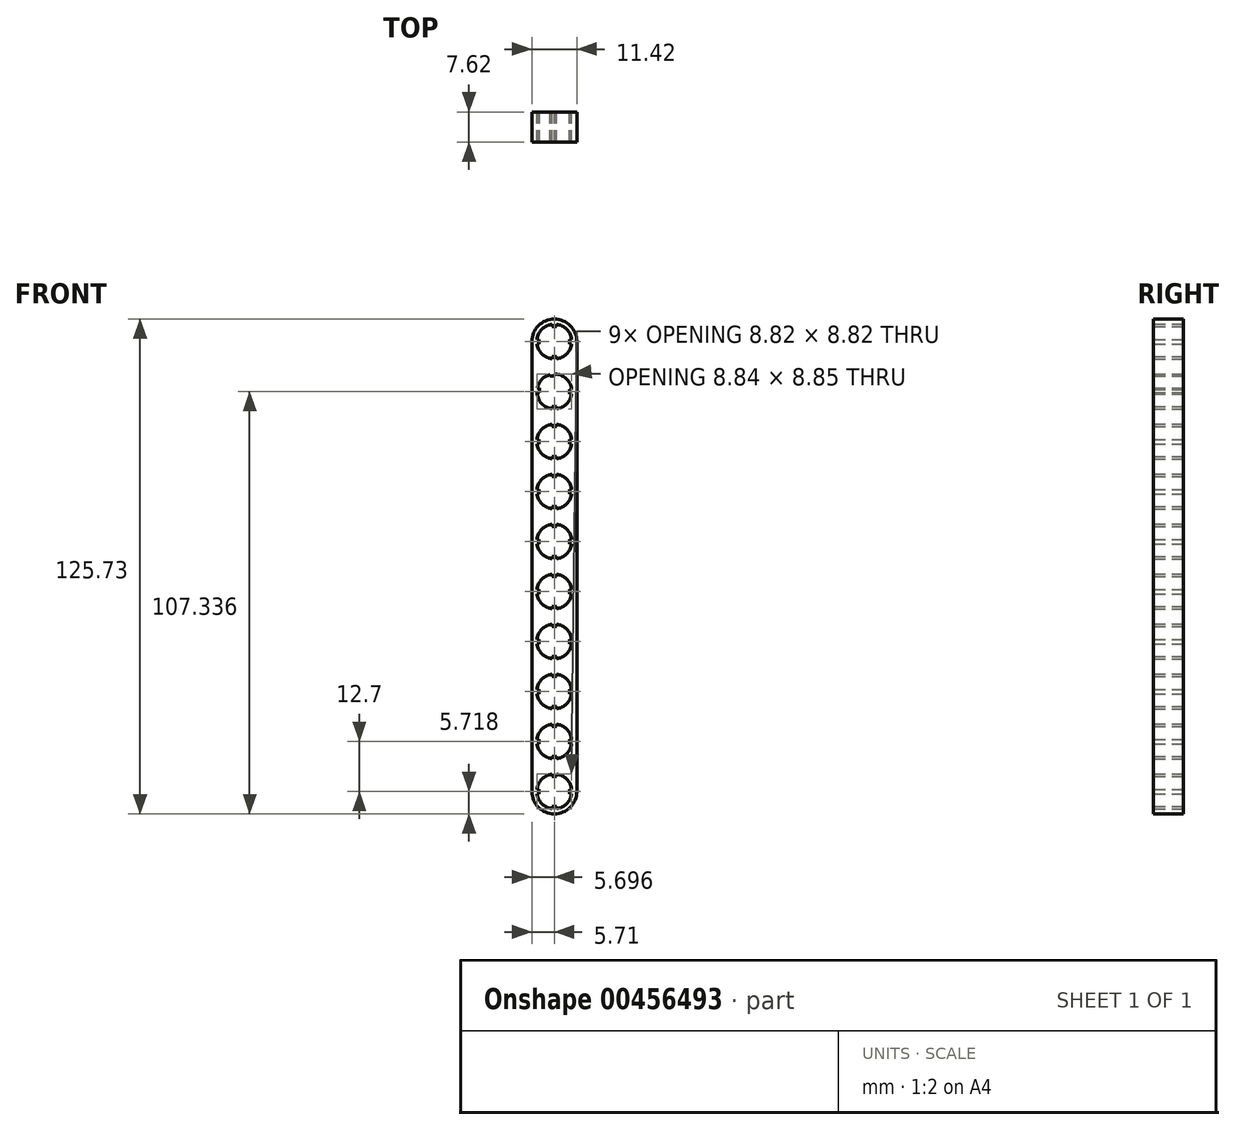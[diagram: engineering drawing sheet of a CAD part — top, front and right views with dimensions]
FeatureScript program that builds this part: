
annotation { "Feature Type Name" : "Feature", "Feature Type Description" : "" }
export const myFeature = defineFeature(function(context is Context, id is Id, definition is map)
    precondition{}
    {
        {
            var Q0;
            Q0=qCreatedBy(makeId("Front.planeOp"),FACE);
            var sketch = newSketch(context, id + "F0", { "sketchPlane" : qUnion([Q0])});
            skCircle(sketch, "E0", {"center": v(0, 47.45) * mm, "radius": 4.45 * mm});
            skCircle(sketch, "E1", {"center": v(0, 34.75) * mm, "radius": 4.45 * mm});
            skCircle(sketch, "E2", {"center": v(0, 22.05) * mm, "radius": 4.45 * mm});
            skCircle(sketch, "E3", {"center": v(0, 9.35) * mm, "radius": 4.45 * mm});
            skCircle(sketch, "E4", {"center": v(0, -3.35) * mm, "radius": 4.45 * mm});
            skCircle(sketch, "E5", {"center": v(0, -16.05) * mm, "radius": 4.45 * mm});
            skCircle(sketch, "E6", {"center": v(0, -28.75) * mm, "radius": 4.45 * mm});
            skCircle(sketch, "E7", {"center": v(0, -41.45) * mm, "radius": 4.45 * mm});
            skCircle(sketch, "E8", {"center": v(0, -54.15) * mm, "radius": 4.45 * mm});
            skCircle(sketch, "E9", {"center": v(0, -66.85) * mm, "radius": 4.45 * mm});
            skCircle(sketch, "E10", {"center": v(0, 47.45) * mm, "radius": 5.72 * mm});
            skCircle(sketch, "E11", {"center": v(0, 34.75) * mm, "radius": 5.72 * mm});
            skCircle(sketch, "E12", {"center": v(0, 22.05) * mm, "radius": 5.72 * mm});
            skCircle(sketch, "E13", {"center": v(0, 9.35) * mm, "radius": 5.72 * mm});
            skCircle(sketch, "E14", {"center": v(0, -3.35) * mm, "radius": 5.72 * mm});
            skCircle(sketch, "E15", {"center": v(0, -16.05) * mm, "radius": 5.72 * mm});
            skCircle(sketch, "E16", {"center": v(0, -28.75) * mm, "radius": 5.72 * mm});
            skCircle(sketch, "E17", {"center": v(0, -41.45) * mm, "radius": 5.72 * mm});
            skCircle(sketch, "E18", {"center": v(0, -54.15) * mm, "radius": 5.72 * mm});
            skCircle(sketch, "E19", {"center": v(0, -66.85) * mm, "radius": 5.72 * mm});
            skLineSegment(sketch, "E20", {"start": v(-5.72, 47.45) * mm, "end": v(-5.71, -66.85) * mm});
            skLineSegment(sketch, "E21", {"start": v(5.72, 47.45) * mm, "end": v(5.72, -66.85) * mm});
            skLineSegment(sketch, "E22", {"start": v(-0.57, 51.86) * mm, "end": v(-0.57, 51.3) * mm});
            skLineSegment(sketch, "E23", {"start": v(-0.57, 51.3) * mm, "end": v(0.57, 51.3) * mm});
            skLineSegment(sketch, "E24", {"start": v(0.57, 51.3) * mm, "end": v(0.57, 51.86) * mm});
            skLineSegment(sketch, "E25", {"start": v(4.4, 48.02) * mm, "end": v(3.85, 48.02) * mm});
            skLineSegment(sketch, "E26", {"start": v(3.85, 48.02) * mm, "end": v(3.85, 46.88) * mm});
            skLineSegment(sketch, "E27", {"start": v(3.85, 46.88) * mm, "end": v(4.4, 46.88) * mm});
            skLineSegment(sketch, "E28", {"start": v(-0.57, 43.04) * mm, "end": v(-0.57, 43.6) * mm});
            skLineSegment(sketch, "E29", {"start": v(-0.57, 43.6) * mm, "end": v(0.57, 43.6) * mm});
            skLineSegment(sketch, "E30", {"start": v(0.57, 43.6) * mm, "end": v(0.57, 43.04) * mm});
            skLineSegment(sketch, "E31", {"start": v(-4.4, 48.02) * mm, "end": v(-3.85, 48.02) * mm});
            skLineSegment(sketch, "E32", {"start": v(-3.85, 48.02) * mm, "end": v(-3.85, 46.88) * mm});
            skLineSegment(sketch, "E33", {"start": v(-3.85, 46.88) * mm, "end": v(-4.4, 46.88) * mm});
            skLineSegment(sketch, "E34", {"start": v(-4.5, -15.48) * mm, "end": v(-3.85, -15.48) * mm});
            skLineSegment(sketch, "E35", {"start": v(-3.85, -15.48) * mm, "end": v(-3.85, -16.62) * mm});
            skLineSegment(sketch, "E36", {"start": v(-3.85, -16.62) * mm, "end": v(-4.4, -16.62) * mm});
            skLineSegment(sketch, "E37", {"start": v(4.4, 9.92) * mm, "end": v(3.85, 9.92) * mm});
            skLineSegment(sketch, "E38", {"start": v(3.85, 9.92) * mm, "end": v(3.85, 8.78) * mm});
            skLineSegment(sketch, "E39", {"start": v(3.85, 8.78) * mm, "end": v(4.4, 8.78) * mm});
            skLineSegment(sketch, "E40", {"start": v(4.4, -66.28) * mm, "end": v(3.85, -66.28) * mm});
            skLineSegment(sketch, "E41", {"start": v(3.85, -66.28) * mm, "end": v(3.85, -67.42) * mm});
            skLineSegment(sketch, "E42", {"start": v(3.85, -67.42) * mm, "end": v(4.4, -67.42) * mm});
            skLineSegment(sketch, "E43", {"start": v(-1.06, 39.07) * mm, "end": v(-1.06, 38.63) * mm});
            skLineSegment(sketch, "E44", {"start": v(-1.06, 38.63) * mm, "end": v(0.09, 38.63) * mm});
            skLineSegment(sketch, "E45", {"start": v(0.09, 38.63) * mm, "end": v(0.09, 39.2) * mm});
            skLineSegment(sketch, "E46", {"start": v(-4.36, 35.61) * mm, "end": v(-3.8, 35.61) * mm});
            skLineSegment(sketch, "E47", {"start": v(-3.8, 35.61) * mm, "end": v(-3.8, 34.47) * mm});
            skLineSegment(sketch, "E48", {"start": v(-3.8, 34.47) * mm, "end": v(-4.44, 34.47) * mm});
            skLineSegment(sketch, "E49", {"start": v(-0.57, 30.34) * mm, "end": v(-0.57, 30.9) * mm});
            skLineSegment(sketch, "E50", {"start": v(-0.57, 30.9) * mm, "end": v(0.57, 30.9) * mm});
            skLineSegment(sketch, "E51", {"start": v(0.57, 30.9) * mm, "end": v(0.57, 30.34) * mm});
            skLineSegment(sketch, "E52", {"start": v(4.4, 35.32) * mm, "end": v(3.85, 35.32) * mm});
            skLineSegment(sketch, "E53", {"start": v(3.85, 35.32) * mm, "end": v(3.85, 34.18) * mm});
            skLineSegment(sketch, "E54", {"start": v(3.85, 34.18) * mm, "end": v(4.4, 34.18) * mm});
            skLineSegment(sketch, "E55", {"start": v(-0.57, 26.46) * mm, "end": v(-0.57, 25.9) * mm});
            skLineSegment(sketch, "E56", {"start": v(-0.57, 25.9) * mm, "end": v(0.57, 25.9) * mm});
            skLineSegment(sketch, "E57", {"start": v(0.57, 25.9) * mm, "end": v(0.57, 26.46) * mm});
            skLineSegment(sketch, "E58", {"start": v(-0.57, 17.64) * mm, "end": v(-0.57, 18.2) * mm});
            skLineSegment(sketch, "E59", {"start": v(-0.57, 18.2) * mm, "end": v(0.57, 18.2) * mm});
            skLineSegment(sketch, "E60", {"start": v(0.57, 18.2) * mm, "end": v(0.57, 17.64) * mm});
            skLineSegment(sketch, "E61", {"start": v(4.4, 22.62) * mm, "end": v(3.85, 22.62) * mm});
            skLineSegment(sketch, "E62", {"start": v(3.85, 22.62) * mm, "end": v(3.85, 21.48) * mm});
            skLineSegment(sketch, "E63", {"start": v(3.85, 21.48) * mm, "end": v(4.4, 21.48) * mm});
            skLineSegment(sketch, "E64", {"start": v(-4.4, 22.62) * mm, "end": v(-3.85, 22.62) * mm});
            skLineSegment(sketch, "E65", {"start": v(-3.85, 22.62) * mm, "end": v(-3.85, 21.48) * mm});
            skLineSegment(sketch, "E66", {"start": v(-3.85, 21.48) * mm, "end": v(-4.4, 21.48) * mm});
            skLineSegment(sketch, "E67", {"start": v(-4.4, 9.92) * mm, "end": v(-3.85, 9.92) * mm});
            skLineSegment(sketch, "E68", {"start": v(-3.85, 9.92) * mm, "end": v(-3.85, 8.78) * mm});
            skLineSegment(sketch, "E69", {"start": v(-3.85, 8.78) * mm, "end": v(-4.4, 8.78) * mm});
            skLineSegment(sketch, "E70", {"start": v(-0.57, 13.76) * mm, "end": v(-0.57, 13.2) * mm});
            skLineSegment(sketch, "E71", {"start": v(-0.57, 13.2) * mm, "end": v(0.57, 13.2) * mm});
            skLineSegment(sketch, "E72", {"start": v(0.57, 13.2) * mm, "end": v(0.57, 13.76) * mm});
            skLineSegment(sketch, "E73", {"start": v(-0.57, 4.94) * mm, "end": v(-0.57, 5.5) * mm});
            skLineSegment(sketch, "E74", {"start": v(-0.57, 5.5) * mm, "end": v(0.57, 5.5) * mm});
            skLineSegment(sketch, "E75", {"start": v(0.57, 5.5) * mm, "end": v(0.57, 4.94) * mm});
            skLineSegment(sketch, "E76", {"start": v(-0.57, 1.06) * mm, "end": v(-0.57, 0.5) * mm});
            skLineSegment(sketch, "E77", {"start": v(-0.57, 0.5) * mm, "end": v(0.57, 0.5) * mm});
            skLineSegment(sketch, "E78", {"start": v(0.57, 0.5) * mm, "end": v(0.57, 1.06) * mm});
            skLineSegment(sketch, "E79", {"start": v(-0.57, -7.76) * mm, "end": v(-0.57, -7.2) * mm});
            skLineSegment(sketch, "E80", {"start": v(-0.57, -7.2) * mm, "end": v(0.57, -7.2) * mm});
            skLineSegment(sketch, "E81", {"start": v(0.57, -7.2) * mm, "end": v(0.57, -7.76) * mm});
            skLineSegment(sketch, "E82", {"start": v(4.4, -2.78) * mm, "end": v(3.85, -2.78) * mm});
            skLineSegment(sketch, "E83", {"start": v(3.85, -2.78) * mm, "end": v(3.85, -3.92) * mm});
            skLineSegment(sketch, "E84", {"start": v(3.85, -3.92) * mm, "end": v(4.4, -3.92) * mm});
            skLineSegment(sketch, "E85", {"start": v(-4.4, -2.78) * mm, "end": v(-3.85, -2.78) * mm});
            skLineSegment(sketch, "E86", {"start": v(-3.85, -2.78) * mm, "end": v(-3.85, -3.92) * mm});
            skLineSegment(sketch, "E87", {"start": v(-3.85, -3.92) * mm, "end": v(-4.4, -3.92) * mm});
            skLineSegment(sketch, "E88", {"start": v(4.4, -15.48) * mm, "end": v(3.85, -15.48) * mm});
            skLineSegment(sketch, "E89", {"start": v(3.85, -15.48) * mm, "end": v(3.85, -16.62) * mm});
            skLineSegment(sketch, "E90", {"start": v(3.85, -16.62) * mm, "end": v(4.4, -16.62) * mm});
            skLineSegment(sketch, "E91", {"start": v(-0.57, -11.64) * mm, "end": v(-0.57, -12.2) * mm});
            skLineSegment(sketch, "E92", {"start": v(-0.57, -12.2) * mm, "end": v(0.57, -12.2) * mm});
            skLineSegment(sketch, "E93", {"start": v(0.57, -12.2) * mm, "end": v(0.57, -11.64) * mm});
            skLineSegment(sketch, "E94", {"start": v(-0.57, -20.46) * mm, "end": v(-0.57, -19.9) * mm});
            skLineSegment(sketch, "E95", {"start": v(-0.57, -19.9) * mm, "end": v(0.57, -19.9) * mm});
            skLineSegment(sketch, "E96", {"start": v(0.57, -19.9) * mm, "end": v(0.57, -20.46) * mm});
            skLineSegment(sketch, "E97", {"start": v(-0.57, -24.34) * mm, "end": v(-0.57, -24.9) * mm});
            skLineSegment(sketch, "E98", {"start": v(-0.57, -24.9) * mm, "end": v(0.57, -24.9) * mm});
            skLineSegment(sketch, "E99", {"start": v(0.57, -24.9) * mm, "end": v(0.57, -24.34) * mm});
            skLineSegment(sketch, "E100", {"start": v(-0.57, -33.16) * mm, "end": v(-0.57, -32.6) * mm});
            skLineSegment(sketch, "E101", {"start": v(-0.57, -32.6) * mm, "end": v(0.57, -32.6) * mm});
            skLineSegment(sketch, "E102", {"start": v(0.57, -32.6) * mm, "end": v(0.57, -33.16) * mm});
            skLineSegment(sketch, "E103", {"start": v(-4.4, -28.18) * mm, "end": v(-3.85, -28.18) * mm});
            skLineSegment(sketch, "E104", {"start": v(-3.85, -28.18) * mm, "end": v(-3.85, -29.32) * mm});
            skLineSegment(sketch, "E105", {"start": v(-3.85, -29.32) * mm, "end": v(-4.4, -29.32) * mm});
            skLineSegment(sketch, "E106", {"start": v(4.4, -28.18) * mm, "end": v(3.85, -28.18) * mm});
            skLineSegment(sketch, "E107", {"start": v(3.85, -28.18) * mm, "end": v(3.85, -29.32) * mm});
            skLineSegment(sketch, "E108", {"start": v(3.85, -29.32) * mm, "end": v(4.4, -29.32) * mm});
            skLineSegment(sketch, "E109", {"start": v(-0.57, -37.04) * mm, "end": v(-0.57, -37.6) * mm});
            skLineSegment(sketch, "E110", {"start": v(-0.57, -37.6) * mm, "end": v(0.57, -37.6) * mm});
            skLineSegment(sketch, "E111", {"start": v(0.57, -37.6) * mm, "end": v(0.57, -37.04) * mm});
            skLineSegment(sketch, "E112", {"start": v(-0.57, -45.86) * mm, "end": v(-0.57, -45.3) * mm});
            skLineSegment(sketch, "E113", {"start": v(-0.57, -45.3) * mm, "end": v(0.57, -45.3) * mm});
            skLineSegment(sketch, "E114", {"start": v(0.57, -45.3) * mm, "end": v(0.57, -45.86) * mm});
            skLineSegment(sketch, "E115", {"start": v(-4.4, -40.88) * mm, "end": v(-3.85, -40.88) * mm});
            skLineSegment(sketch, "E116", {"start": v(-3.85, -40.88) * mm, "end": v(-3.85, -42.02) * mm});
            skLineSegment(sketch, "E117", {"start": v(-3.85, -42.02) * mm, "end": v(-4.4, -42.02) * mm});
            skLineSegment(sketch, "E118", {"start": v(4.4, -40.88) * mm, "end": v(3.85, -40.88) * mm});
            skLineSegment(sketch, "E119", {"start": v(3.85, -40.88) * mm, "end": v(3.85, -42.02) * mm});
            skLineSegment(sketch, "E120", {"start": v(3.85, -42.02) * mm, "end": v(4.4, -42.02) * mm});
            skLineSegment(sketch, "E121", {"start": v(-0.57, -49.74) * mm, "end": v(-0.57, -50.3) * mm});
            skLineSegment(sketch, "E122", {"start": v(-0.57, -50.3) * mm, "end": v(0.57, -50.3) * mm});
            skLineSegment(sketch, "E123", {"start": v(0.57, -50.3) * mm, "end": v(0.57, -49.74) * mm});
            skLineSegment(sketch, "E124", {"start": v(-0.57, -58.56) * mm, "end": v(-0.57, -58) * mm});
            skLineSegment(sketch, "E125", {"start": v(-0.57, -58) * mm, "end": v(0.57, -58) * mm});
            skLineSegment(sketch, "E126", {"start": v(0.57, -58) * mm, "end": v(0.57, -58.56) * mm});
            skLineSegment(sketch, "E127", {"start": v(-4.4, -53.58) * mm, "end": v(-3.85, -53.58) * mm});
            skLineSegment(sketch, "E128", {"start": v(-3.85, -53.58) * mm, "end": v(-3.85, -54.72) * mm});
            skLineSegment(sketch, "E129", {"start": v(-3.85, -54.72) * mm, "end": v(-4.4, -54.72) * mm});
            skLineSegment(sketch, "E130", {"start": v(4.4, -53.58) * mm, "end": v(3.85, -53.58) * mm});
            skLineSegment(sketch, "E131", {"start": v(3.85, -53.58) * mm, "end": v(3.85, -54.72) * mm});
            skLineSegment(sketch, "E132", {"start": v(3.85, -54.72) * mm, "end": v(4.4, -54.72) * mm});
            skLineSegment(sketch, "E133", {"start": v(-4.4, -66.28) * mm, "end": v(-3.85, -66.28) * mm});
            skLineSegment(sketch, "E134", {"start": v(-3.85, -66.28) * mm, "end": v(-3.85, -67.42) * mm});
            skLineSegment(sketch, "E135", {"start": v(-3.85, -67.42) * mm, "end": v(-4.4, -67.42) * mm});
            skLineSegment(sketch, "E136", {"start": v(-0.57, -62.44) * mm, "end": v(-0.57, -63) * mm});
            skLineSegment(sketch, "E137", {"start": v(-0.57, -63) * mm, "end": v(0.57, -63) * mm});
            skLineSegment(sketch, "E138", {"start": v(0.57, -63) * mm, "end": v(0.57, -62.44) * mm});
            skLineSegment(sketch, "E139", {"start": v(-0.57, -71.26) * mm, "end": v(-0.57, -70.7) * mm});
            skLineSegment(sketch, "E140", {"start": v(-0.57, -70.7) * mm, "end": v(0.57, -70.7) * mm});
            skLineSegment(sketch, "E141", {"start": v(0.57, -70.7) * mm, "end": v(0.57, -71.26) * mm});
            skSolve(sketch);
        }
        {
            var Q0;
            Q0 = qSketchRegion(id + "F0", true);
            var Q1;
            {var subQ0=sQuery(id+"F0.wireOp",EDGE,"E22");Q1=makeQuery(id+"F0.imprint","IMPRINT",FACE,{"disambiguationData":[TD([[makeQuery(id+"F0.imprint","IMPRINT",EDGE,{"derivedFrom":subQ0}),1.0]])]});}
            var Q2;
            {var subQ0=sQuery(id+"F0.wireOp",EDGE,"E25");Q2=makeQuery(id+"F0.imprint","IMPRINT",FACE,{"disambiguationData":[TD([[makeQuery(id+"F0.imprint","IMPRINT",EDGE,{"derivedFrom":subQ0}),1.0]])]});}
            var Q3;
            {var subQ0=sQuery(id+"F0.wireOp",EDGE,"E28");Q3=makeQuery(id+"F0.imprint","IMPRINT",FACE,{"disambiguationData":[TD([[makeQuery(id+"F0.imprint","IMPRINT",EDGE,{"derivedFrom":subQ0}),-1.0]])]});}
            var Q4;
            {var subQ0=sQuery(id+"F0.wireOp",EDGE,"E31");Q4=makeQuery(id+"F0.imprint","IMPRINT",FACE,{"disambiguationData":[TD([[makeQuery(id+"F0.imprint","IMPRINT",EDGE,{"derivedFrom":subQ0}),-1.0]])]});}
            var Q5;
            {var subQ4=sQuery(id+"F0.wireOp",EDGE,"E41");Q5=makeQuery(id+"F0.imprint","IMPRINT",FACE,{"disambiguationData":[TD([[makeQuery(id+"F0.imprint","IMPRINT",EDGE,{"derivedFrom":subQ4}),1.0]])]});}
            var Q6;
            {var subQ0=sQuery(id+"F0.wireOp",EDGE,"e1f3bca3-39cc-4dae-b2d7-83d18609ecb4");Q6=makeQuery(id+"F0.imprint","IMPRINT",FACE,{"disambiguationData":[TD([[makeQuery(id+"F0.imprint","IMPRINT",EDGE,{"derivedFrom":subQ0}),-1.0]])]});}
            var Q7;
            {var subQ0=sQuery(id+"F0.wireOp",EDGE,"910688c2-77c3-4042-a3fa-0c8df72c775e");Q7=makeQuery(id+"F0.imprint","IMPRINT",FACE,{"disambiguationData":[TD([[makeQuery(id+"F0.imprint","IMPRINT",EDGE,{"derivedFrom":subQ0}),-1.0]])]});}
            var Q8;
            {var subQ0=sQuery(id+"F0.wireOp",EDGE,"E37");Q8=makeQuery(id+"F0.imprint","IMPRINT",FACE,{"disambiguationData":[TD([[makeQuery(id+"F0.imprint","IMPRINT",EDGE,{"derivedFrom":subQ0}),1.0]])]});}
            var Q9;
            {var subQ0=sQuery(id+"F0.wireOp",EDGE,"63ec64b3-a681-4c96-b772-ad6f1b6ddcf5");Q9=makeQuery(id+"F0.imprint","IMPRINT",FACE,{"disambiguationData":[TD([[makeQuery(id+"F0.imprint","IMPRINT",EDGE,{"derivedFrom":subQ0}),-1.0]])]});}
            var Q10;
            {var subQ4=sQuery(id+"F0.wireOp",EDGE,"E35");Q10=makeQuery(id+"F0.imprint","IMPRINT",FACE,{"disambiguationData":[TD([[makeQuery(id+"F0.imprint","IMPRINT",EDGE,{"derivedFrom":subQ4}),-1.0]])]});}
            var Q11;
            {var subQ0=sQuery(id+"F0.wireOp",EDGE,"E43");Q11=makeQuery(id+"F0.imprint","IMPRINT",FACE,{"disambiguationData":[TD([[makeQuery(id+"F0.imprint","IMPRINT",EDGE,{"derivedFrom":subQ0}),1.0]])]});}
            var Q12;
            {var subQ0=sQuery(id+"F0.wireOp",EDGE,"E46");Q12=makeQuery(id+"F0.imprint","IMPRINT",FACE,{"disambiguationData":[TD([[makeQuery(id+"F0.imprint","IMPRINT",EDGE,{"derivedFrom":subQ0}),-1.0]])]});}
            var Q13;
            {var subQ0=sQuery(id+"F0.wireOp",EDGE,"E49");Q13=makeQuery(id+"F0.imprint","IMPRINT",FACE,{"disambiguationData":[TD([[makeQuery(id+"F0.imprint","IMPRINT",EDGE,{"derivedFrom":subQ0}),-1.0]])]});}
            var Q14;
            {var subQ0=sQuery(id+"F0.wireOp",EDGE,"E52");Q14=makeQuery(id+"F0.imprint","IMPRINT",FACE,{"disambiguationData":[TD([[makeQuery(id+"F0.imprint","IMPRINT",EDGE,{"derivedFrom":subQ0}),1.0]])]});}
            var Q15;
            {var subQ0=sQuery(id+"F0.wireOp",EDGE,"E55");Q15=makeQuery(id+"F0.imprint","IMPRINT",FACE,{"disambiguationData":[TD([[makeQuery(id+"F0.imprint","IMPRINT",EDGE,{"derivedFrom":subQ0}),1.0]])]});}
            var Q16;
            {var subQ0=sQuery(id+"F0.wireOp",EDGE,"E64");Q16=makeQuery(id+"F0.imprint","IMPRINT",FACE,{"disambiguationData":[TD([[makeQuery(id+"F0.imprint","IMPRINT",EDGE,{"derivedFrom":subQ0}),-1.0]])]});}
            var Q17;
            {var subQ0=sQuery(id+"F0.wireOp",EDGE,"E61");Q17=makeQuery(id+"F0.imprint","IMPRINT",FACE,{"disambiguationData":[TD([[makeQuery(id+"F0.imprint","IMPRINT",EDGE,{"derivedFrom":subQ0}),1.0]])]});}
            var Q18;
            {var subQ0=sQuery(id+"F0.wireOp",EDGE,"E58");Q18=makeQuery(id+"F0.imprint","IMPRINT",FACE,{"disambiguationData":[TD([[makeQuery(id+"F0.imprint","IMPRINT",EDGE,{"derivedFrom":subQ0}),-1.0]])]});}
            var Q19;
            {var subQ0=sQuery(id+"F0.wireOp",EDGE,"E70");Q19=makeQuery(id+"F0.imprint","IMPRINT",FACE,{"disambiguationData":[TD([[makeQuery(id+"F0.imprint","IMPRINT",EDGE,{"derivedFrom":subQ0}),1.0]])]});}
            var Q20;
            {var subQ0=sQuery(id+"F0.wireOp",EDGE,"E67");Q20=makeQuery(id+"F0.imprint","IMPRINT",FACE,{"disambiguationData":[TD([[makeQuery(id+"F0.imprint","IMPRINT",EDGE,{"derivedFrom":subQ0}),-1.0]])]});}
            var Q21;
            {var subQ0=sQuery(id+"F0.wireOp",EDGE,"E73");Q21=makeQuery(id+"F0.imprint","IMPRINT",FACE,{"disambiguationData":[TD([[makeQuery(id+"F0.imprint","IMPRINT",EDGE,{"derivedFrom":subQ0}),-1.0]])]});}
            var Q22;
            {var subQ0=sQuery(id+"F0.wireOp",EDGE,"E76");Q22=makeQuery(id+"F0.imprint","IMPRINT",FACE,{"disambiguationData":[TD([[makeQuery(id+"F0.imprint","IMPRINT",EDGE,{"derivedFrom":subQ0}),1.0]])]});}
            var Q23;
            {var subQ0=sQuery(id+"F0.wireOp",EDGE,"E82");Q23=makeQuery(id+"F0.imprint","IMPRINT",FACE,{"disambiguationData":[TD([[makeQuery(id+"F0.imprint","IMPRINT",EDGE,{"derivedFrom":subQ0}),1.0]])]});}
            var Q24;
            {var subQ0=sQuery(id+"F0.wireOp",EDGE,"E79");Q24=makeQuery(id+"F0.imprint","IMPRINT",FACE,{"disambiguationData":[TD([[makeQuery(id+"F0.imprint","IMPRINT",EDGE,{"derivedFrom":subQ0}),-1.0]])]});}
            var Q25;
            {var subQ0=sQuery(id+"F0.wireOp",EDGE,"E85");Q25=makeQuery(id+"F0.imprint","IMPRINT",FACE,{"disambiguationData":[TD([[makeQuery(id+"F0.imprint","IMPRINT",EDGE,{"derivedFrom":subQ0}),-1.0]])]});}
            var Q26;
            {var subQ0=sQuery(id+"F0.wireOp",EDGE,"E91");Q26=makeQuery(id+"F0.imprint","IMPRINT",FACE,{"disambiguationData":[TD([[makeQuery(id+"F0.imprint","IMPRINT",EDGE,{"derivedFrom":subQ0}),1.0]])]});}
            var Q27;
            {var subQ0=sQuery(id+"F0.wireOp",EDGE,"E88");Q27=makeQuery(id+"F0.imprint","IMPRINT",FACE,{"disambiguationData":[TD([[makeQuery(id+"F0.imprint","IMPRINT",EDGE,{"derivedFrom":subQ0}),1.0]])]});}
            var Q28;
            {var subQ0=sQuery(id+"F0.wireOp",EDGE,"E94");Q28=makeQuery(id+"F0.imprint","IMPRINT",FACE,{"disambiguationData":[TD([[makeQuery(id+"F0.imprint","IMPRINT",EDGE,{"derivedFrom":subQ0}),-1.0]])]});}
            var Q29;
            {var subQ0=sQuery(id+"F0.wireOp",EDGE,"E97");Q29=makeQuery(id+"F0.imprint","IMPRINT",FACE,{"disambiguationData":[TD([[makeQuery(id+"F0.imprint","IMPRINT",EDGE,{"derivedFrom":subQ0}),1.0]])]});}
            var Q30;
            {var subQ0=sQuery(id+"F0.wireOp",EDGE,"E106");Q30=makeQuery(id+"F0.imprint","IMPRINT",FACE,{"disambiguationData":[TD([[makeQuery(id+"F0.imprint","IMPRINT",EDGE,{"derivedFrom":subQ0}),1.0]])]});}
            var Q31;
            {var subQ0=sQuery(id+"F0.wireOp",EDGE,"E103");Q31=makeQuery(id+"F0.imprint","IMPRINT",FACE,{"disambiguationData":[TD([[makeQuery(id+"F0.imprint","IMPRINT",EDGE,{"derivedFrom":subQ0}),-1.0]])]});}
            var Q32;
            {var subQ0=sQuery(id+"F0.wireOp",EDGE,"E100");Q32=makeQuery(id+"F0.imprint","IMPRINT",FACE,{"disambiguationData":[TD([[makeQuery(id+"F0.imprint","IMPRINT",EDGE,{"derivedFrom":subQ0}),-1.0]])]});}
            var Q33;
            {var subQ0=sQuery(id+"F0.wireOp",EDGE,"E109");Q33=makeQuery(id+"F0.imprint","IMPRINT",FACE,{"disambiguationData":[TD([[makeQuery(id+"F0.imprint","IMPRINT",EDGE,{"derivedFrom":subQ0}),1.0]])]});}
            var Q34;
            {var subQ0=sQuery(id+"F0.wireOp",EDGE,"E118");Q34=makeQuery(id+"F0.imprint","IMPRINT",FACE,{"disambiguationData":[TD([[makeQuery(id+"F0.imprint","IMPRINT",EDGE,{"derivedFrom":subQ0}),1.0]])]});}
            var Q35;
            {var subQ0=sQuery(id+"F0.wireOp",EDGE,"E115");Q35=makeQuery(id+"F0.imprint","IMPRINT",FACE,{"disambiguationData":[TD([[makeQuery(id+"F0.imprint","IMPRINT",EDGE,{"derivedFrom":subQ0}),-1.0]])]});}
            var Q36;
            {var subQ0=sQuery(id+"F0.wireOp",EDGE,"E112");Q36=makeQuery(id+"F0.imprint","IMPRINT",FACE,{"disambiguationData":[TD([[makeQuery(id+"F0.imprint","IMPRINT",EDGE,{"derivedFrom":subQ0}),-1.0]])]});}
            var Q37;
            {var subQ0=sQuery(id+"F0.wireOp",EDGE,"E121");Q37=makeQuery(id+"F0.imprint","IMPRINT",FACE,{"disambiguationData":[TD([[makeQuery(id+"F0.imprint","IMPRINT",EDGE,{"derivedFrom":subQ0}),1.0]])]});}
            var Q38;
            {var subQ0=sQuery(id+"F0.wireOp",EDGE,"E130");Q38=makeQuery(id+"F0.imprint","IMPRINT",FACE,{"disambiguationData":[TD([[makeQuery(id+"F0.imprint","IMPRINT",EDGE,{"derivedFrom":subQ0}),1.0]])]});}
            var Q39;
            {var subQ0=sQuery(id+"F0.wireOp",EDGE,"E124");Q39=makeQuery(id+"F0.imprint","IMPRINT",FACE,{"disambiguationData":[TD([[makeQuery(id+"F0.imprint","IMPRINT",EDGE,{"derivedFrom":subQ0}),-1.0]])]});}
            var Q40;
            {var subQ0=sQuery(id+"F0.wireOp",EDGE,"E127");Q40=makeQuery(id+"F0.imprint","IMPRINT",FACE,{"disambiguationData":[TD([[makeQuery(id+"F0.imprint","IMPRINT",EDGE,{"derivedFrom":subQ0}),-1.0]])]});}
            var Q41;
            {var subQ0=sQuery(id+"F0.wireOp",EDGE,"E136");Q41=makeQuery(id+"F0.imprint","IMPRINT",FACE,{"disambiguationData":[TD([[makeQuery(id+"F0.imprint","IMPRINT",EDGE,{"derivedFrom":subQ0}),1.0]])]});}
            var Q42;
            {var subQ0=sQuery(id+"F0.wireOp",EDGE,"E133");Q42=makeQuery(id+"F0.imprint","IMPRINT",FACE,{"disambiguationData":[TD([[makeQuery(id+"F0.imprint","IMPRINT",EDGE,{"derivedFrom":subQ0}),-1.0]])]});}
            var Q43;
            {var subQ0=sQuery(id+"F0.wireOp",EDGE,"E139");Q43=makeQuery(id+"F0.imprint","IMPRINT",FACE,{"disambiguationData":[TD([[makeQuery(id+"F0.imprint","IMPRINT",EDGE,{"derivedFrom":subQ0}),-1.0]])]});}
            extrude(context, id + "F1", {"entities" : qUnion([Q0, Q1, Q2, Q3, Q4, Q5, Q6, Q7, Q8, Q9, Q10, Q11, Q12, Q13, Q14, Q15, Q16, Q17, Q18, Q19, Q20, Q21, Q22, Q23, Q24, Q25, Q26, Q27, Q28, Q29, Q30, Q31, Q32, Q33, Q34, Q35, Q36, Q37, Q38, Q39, Q40, Q41, Q42, Q43]), "depth" : 7.62 * mm, "offsetDistance" : 25.4 * mm});
        }
    });
